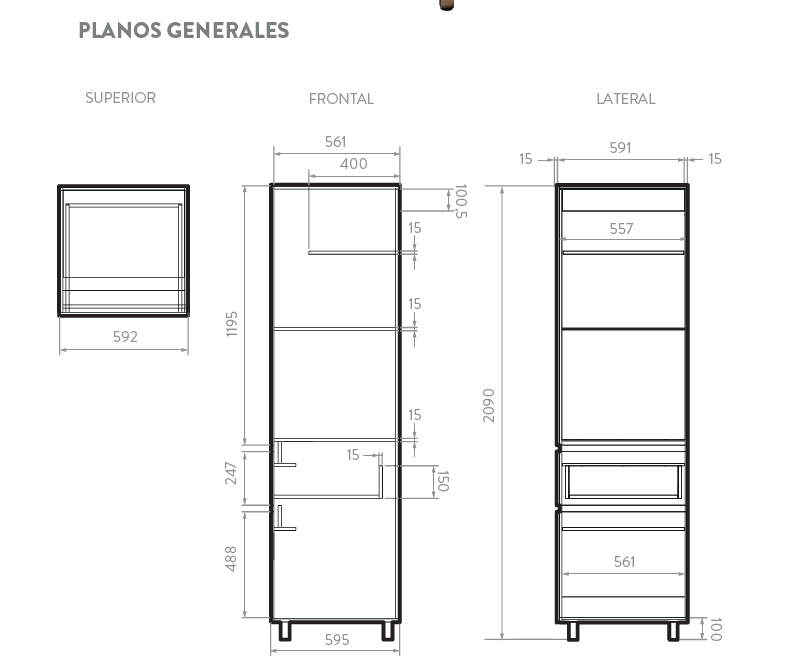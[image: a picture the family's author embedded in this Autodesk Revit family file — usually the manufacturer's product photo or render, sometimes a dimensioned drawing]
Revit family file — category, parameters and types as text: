
# Revit family: 125521711_Alacena Soho
name_source: partatom
category: Mobiliario
units: mm (PartAtom-declared; Revit-internal decimal feet)

## family parameters
Compartido = No
Corte con vacíos al cargar = No
Número OmniClass = 23.21.23.39
Punto de cálculo de habitación = No
Se basa en plano de trabajo = No
Siempre vertical = Sí
Título OmniClass = Residential Kitchen and Dining Room Furniture

## types (1)
- Ref. 125521711 MIEL + PLOMO
    Alto = 2090 mm  [stored 6.85696 ft]
    Ancho = 592 mm  [stored 1.94226 ft]
    Carga Máxima = 70 kg.
    Densidad = 15 mms 670 kg./m^3.
3 mms 742 kg./m^3.
    Descripción = Complemento ideal para la Cocina Soho brindando un espacio
adicional de almacenamiento. Cuenta con gabinete superior y dos cajones
inferiores para tener siempre a la mano los elementos de cocina y alimentos.
    Dimensiones generales producto (H * W * D) = H 2090 x W 592 x L 595 mm.
    Fabricante = Corona
    Garantia mueble y herrajes = 1 año
    Material estructura = Corona_Madera_Blanco
    Material patas = Corona_Acero
    Material pieza interior = Corona_Madera_Aglomerada_Plomo
    Material puertas = Corona_Madera_Aglomerada_Miel
    Peso Neto aprox = 61.5 kg.
    Profundidad = 595 mm
    Resistencia a la humedad = Hinchamiento < o =8%.
    URL = https://corona.co

note: [stored X ft] marks values corroborated as IEEE doubles in the binary element streams (Revit-internal decimal feet)

## geometry (parser evidence)
native form markers: Blend x3, Extrusion x1, Sweep x4
no freeform markers — native parametric forms only
